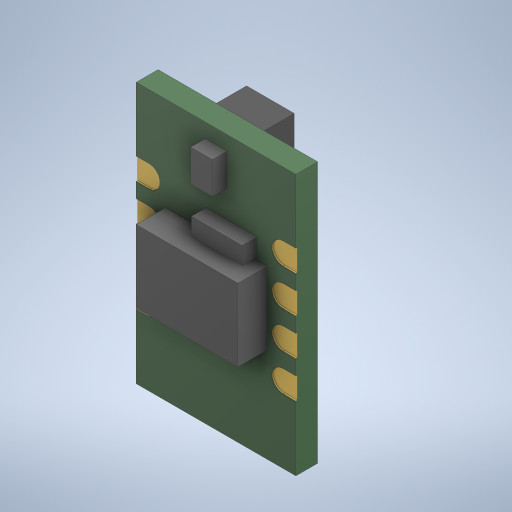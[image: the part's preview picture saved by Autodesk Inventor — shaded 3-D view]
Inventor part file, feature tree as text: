
AUTODESK INVENTOR PART (.ipt)
format: ipt  version: 2024.1 (Build 281209000, 209)  size: 1,507,328 bytes
history: native  units: mm
features: extrude x8, sketch x7, projected_geometry x2, other x1, imported_body x1
ambient origin geometry x8: Origin, YZ Plane, XZ Plane, XY Plane, X Axis, Y Axis, Z Axis, Center Point
bodies: Body1 (feature_tree)
feature tree (19):
  other  "ソリッド1"
  extrude  "押し出し1"  Depth=1.5mm TaperAngle=0.0deg
  extrude  "押し出し2"  Depth=11.0mm
  sketch  "スケッチ3"
  extrude  "押し出し3"  Depth=18.0mm
  extrude  "押し出し4"  Depth=1.5mm TaperAngle=0.0deg
  extrude  "押し出し5"  Depth=2.0mm
  extrude  "押し出し6"  Depth=5.0mm
  extrude  "押し出し7"  Depth=1.5mm
  extrude  "押し出し9"  Depth=2.2mm
  sketch  "スケッチ1"
  sketch  "スケッチ2"
  sketch  "スケッチ4"
  sketch  "スケッチ5"
  projected_geometry  "投影ループ1"
  sketch  "スケッチ6"
  projected_geometry  "投影ループ2"
  sketch  "スケッチ7"
  imported_body  "Base1"
